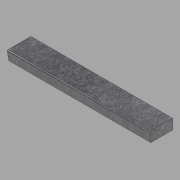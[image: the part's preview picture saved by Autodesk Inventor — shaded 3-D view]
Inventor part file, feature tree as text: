
AUTODESK INVENTOR PART (.ipt)
format: ipt  version: 2022.1 (Build 261234020, 234B)  size: 117,760 bytes
history: native  units: in
note: dims shown in document units (in); Inventor stores cm internally (conversion verified against a paired STEP export)
features: other x3, extrude x1, sketch x1
ambient origin geometry x8: Origin, YZ Plane, XZ Plane, XY Plane, X Axis, Y Axis, Z Axis, Center Point
bodies: Solid1 (feature_tree)
feature tree (5):
  other  "Blocks"
  extrude  "Extrusion1"  Depth=83.875in TaperAngle=0.0deg
  sketch  "Sketch1"  dims[d0=13.0in d1=6.0in d2=13.5in d3=0.5in d4=0.5in d5=83.875in d6=0.0in]
  other  "Profile"
  other  "Profile:1"
